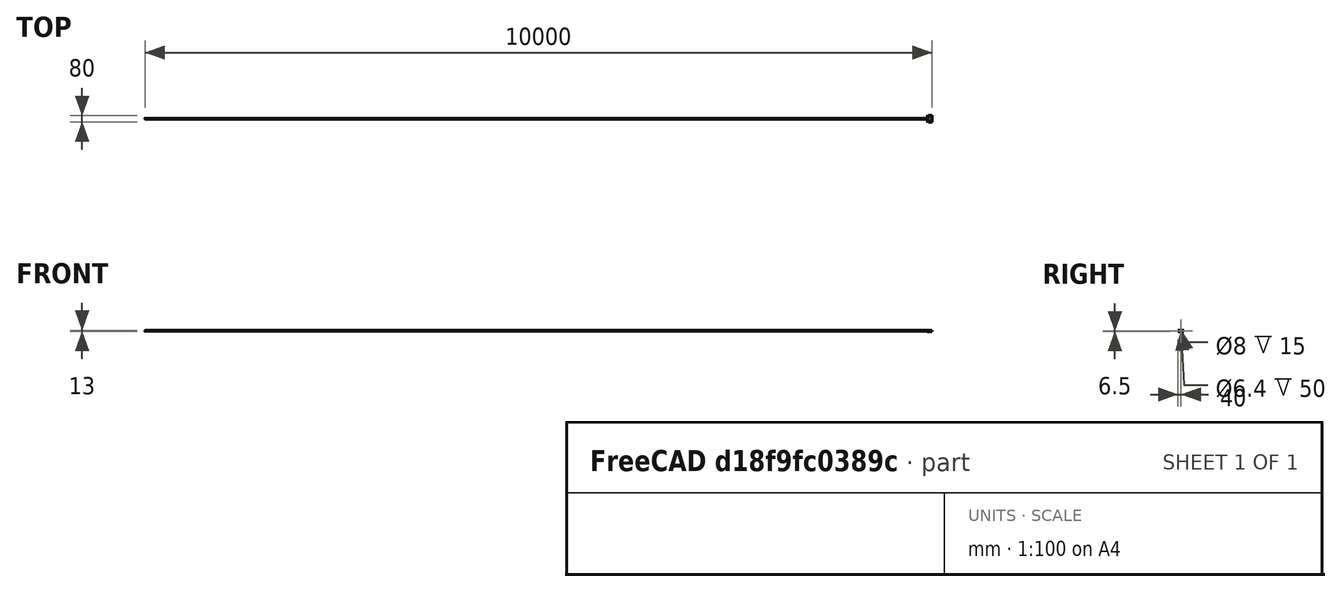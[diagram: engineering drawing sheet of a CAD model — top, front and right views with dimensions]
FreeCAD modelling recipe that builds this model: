
FCSTD DOCUMENT  (FreeCAD 0.16R)
Label: Mk1_1
License: All rights reserved
LicenseURL: http://en.wikipedia.org/wiki/All_rights_reserved
objects: Sketcher::SketchObject×3, PartDesign::Pocket×2, PartDesign::Pad×1, PartDesign::Fillet×1, PartDesign::Chamfer×1, Mesh::Feature×1
note: 11 computed .brp shape members not serialized (recipe doc carries the construction recipe); baked Part::Feature solids carry a one-line shape summary decoded from their .brp

FEATURE [Sketcher::SketchObject] Sketch
  sketch-geometry (7):
    g0: LineSegment StartX=25 StartY=40 StartZ=0 EndX=25 EndY=-40 EndZ=0
    g1: LineSegment StartX=-40 StartY=10 StartZ=0 EndX=-20 EndY=40 EndZ=0
    g2: LineSegment StartX=-20 StartY=40 StartZ=0 EndX=25 EndY=40 EndZ=0
    g3: LineSegment StartX=25 StartY=40 StartZ=0 EndX=25 EndY=-40 EndZ=0
    g4: LineSegment StartX=25 StartY=-40 StartZ=0 EndX=-20 EndY=-40 EndZ=0
    g5: LineSegment StartX=-20 StartY=-40 StartZ=0 EndX=-40 EndY=-10 EndZ=0
    g6: LineSegment StartX=-40 StartY=-10 StartZ=0 EndX=-40 EndY=10 EndZ=0
  constraints (19):
    c: Coincident(g1,g2)
    c: Horizontal(g2)
    c: Coincident(g2,g3)
    c: Coincident(g3,g0)
    c: Vertical(g3)
    c: Coincident(g3,g4)
    c: Horizontal(g4)
    c: Coincident(g4,g5)
    c: Coincident(g5,g6)
    c: Coincident(g0,g2)
    c: Coincident(g1,g6)
    c: Distance(g-1,g0) = 25
    c: DistanceX(g1,g-1) = 20
    c: DistanceX(g1,g-1) = 40
    c: Vertical(g6)
    c: Symmetric(g1,g5,g-1)
    c: Symmetric(g4,g1,g-1)
    c: DistanceY(g1) = 10
    c: Distance(g0) = 80
FEATURE [PartDesign::Pad] Pad
  Length = 13
  Length2 = 100
  Sketch = -> Sketch
  Type = 0
FEATURE [Sketcher::SketchObject] Sketch001
  ExternalGeometry = -> [Pad]
  Placement = pos=(25,0,0) rot=(0.57735,0.57735,0.57735;2.0944rad)
  Support = -> Pad [Face1]
  sketch-geometry (1):
    g0: Circle CenterX=0 CenterY=6.5 CenterZ=0 NormalX=0 NormalY=0 NormalZ=1 Radius=3.2
  constraints (2):
    c: Symmetric(g-3,g-4,g0)
    c: Radius(g0) = 3.2
FEATURE [PartDesign::Pocket] Pocket
  Length = 20
  Sketch = -> Sketch001
  Type = 1
FEATURE [Sketcher::SketchObject] Sketch002
  ExternalGeometry = -> [Pocket]
  Placement = pos=(25,0,0) rot=(0.57735,0.57735,0.57735;2.0944rad)
  Support = -> Pocket [Face1]
  sketch-geometry (1):
    g0: Circle CenterX=0 CenterY=6.5 CenterZ=0 NormalX=0 NormalY=0 NormalZ=1 Radius=4
  constraints (2):
    c: Symmetric(g-4,g-3,g0)
    c: Radius(g0) = 4
FEATURE [PartDesign::Pocket] Pocket001
  Length = 15
  Sketch = -> Sketch002
  Type = 0
FEATURE [PartDesign::Fillet] Fillet
  Base = -> Pocket001 [Edge4,Edge17,Edge21,Edge20,Edge6,Edge1]
  Radius = 10
FEATURE [PartDesign::Chamfer] Chamfer
  Base = -> Fillet [Edge1,Edge6,Edge7,Edge8,Edge9,Edge10,Edge11,Edge12,Edge13,Edge14,Edge15,Edge16,Edge4,Edge18,Edge20,Edge21,Edge22,Edge23,Edge24,Edge25,Edge26,Edge27,Edge28,Edge29]
  Size = 1
FEATURE [Mesh::Feature] Mesh  label="Chamfer (Meshed)"
